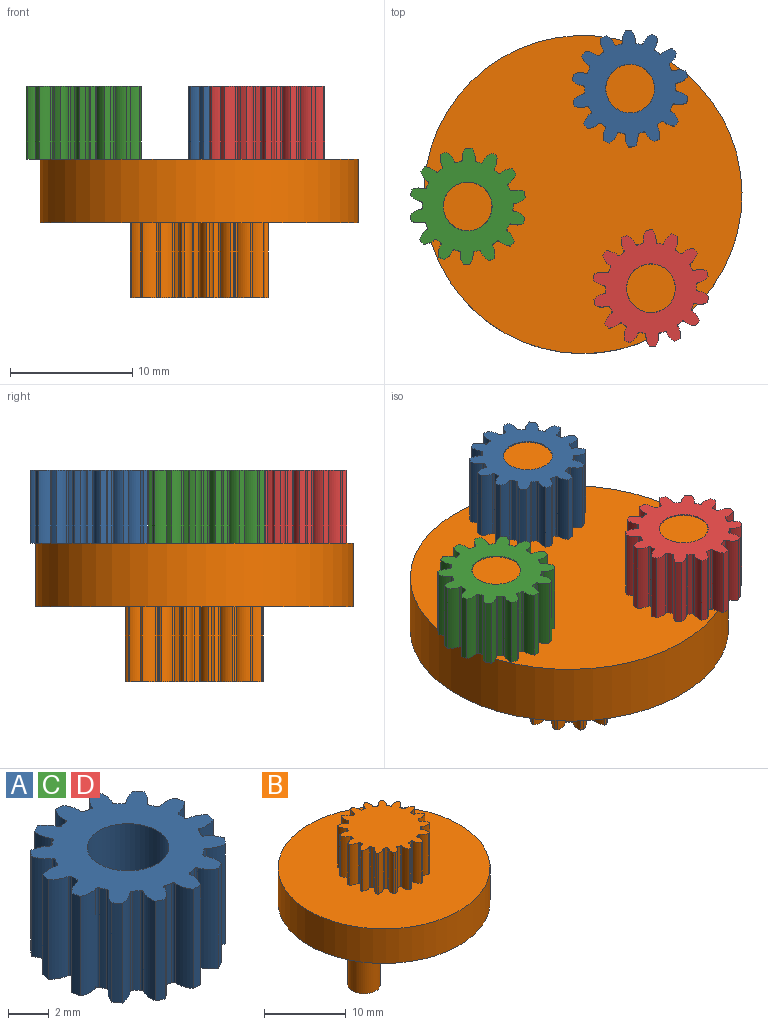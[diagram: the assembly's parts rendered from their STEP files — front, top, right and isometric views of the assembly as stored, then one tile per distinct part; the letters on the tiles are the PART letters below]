
ASSEMBLY  parts=4 mates=3
PART A: 87 faces, bbox 9.4x9.5x5.9 mm
  f0: cylinder r=0.13mm len=5.94mm, axis (0,0,-1), area 1.1mm2, adj f1,f84,f85,f86
  f1: cylinder r=3.71mm len=5.94mm, axis (0,0,-1), area 2.3mm2, adj f0,f2,f85,f86
  f2: cylinder r=0.13mm len=5.94mm, axis (0,0,-1), area 1.1mm2, adj f1,f3,f85,f86
  f3: cylinder r=1.52mm len=5.94mm, axis (0,0,-1), area 6.1mm2, adj f2,f4,f85,f86
  f4: cylinder r=4.76mm len=5.94mm, axis (0,0,-1), area 3mm2, adj f3,f5,f85,f86
  f5: cylinder r=1.52mm len=5.94mm, axis (0,0,-1), area 6.1mm2, adj f4,f6,f85,f86
  f6: cylinder r=0.13mm len=5.94mm, axis (0,0,-1), area 1.1mm2, adj f5,f7,f85,f86
  f7: cylinder r=3.71mm len=5.94mm, axis (0,0,-1), area 2.3mm2, adj f6,f8,f85,f86
  f8: cylinder r=0.13mm len=5.94mm, axis (0,0,-1), area 1.1mm2, adj f7,f9,f85,f86
  f9: cylinder r=1.52mm len=5.94mm, axis (0,0,-1), area 6.1mm2, adj f8,f10,f85,f86
  f10: cylinder r=4.76mm len=5.94mm, axis (0,0,-1), area 3mm2, adj f9,f11,f85,f86
  f11: cylinder r=1.52mm len=5.94mm, axis (0,0,-1), area 6.1mm2, adj f10,f12,f85,f86
  f12: cylinder r=0.13mm len=5.94mm, axis (0,0,-1), area 1.1mm2, adj f11,f13,f85,f86
  f13: cylinder r=3.71mm len=5.94mm, axis (0,0,-1), area 2.3mm2, adj f12,f14,f85,f86
  f14: cylinder r=0.13mm len=5.94mm, axis (0,0,-1), area 1.1mm2, adj f13,f15,f85,f86
  f15: cylinder r=1.52mm len=5.94mm, axis (0,0,-1), area 6.1mm2, adj f14,f16,f85,f86
  f16: cylinder r=4.76mm len=5.94mm, axis (0,0,-1), area 3mm2, adj f15,f17,f85,f86
  f17: cylinder r=1.52mm len=5.94mm, axis (0,0,-1), area 6.1mm2, adj f16,f18,f85,f86
  f18: cylinder r=0.13mm len=5.94mm, axis (0,0,-1), area 1.1mm2, adj f17,f19,f85,f86
  f19: cylinder r=3.71mm len=5.94mm, axis (0,0,-1), area 2.3mm2, adj f18,f20,f85,f86
  f20: cylinder r=0.13mm len=5.94mm, axis (0,0,-1), area 1.1mm2, adj f19,f21,f85,f86
  f21: cylinder r=1.52mm len=5.94mm, axis (0,0,-1), area 6.1mm2, adj f20,f22,f85,f86
  f22: cylinder r=4.76mm len=5.94mm, axis (0,0,-1), area 3mm2, adj f21,f23,f85,f86
  f23: cylinder r=1.52mm len=5.94mm, axis (0,0,-1), area 6.1mm2, adj f22,f24,f85,f86
  f24: cylinder r=0.13mm len=5.94mm, axis (0,0,-1), area 1.1mm2, adj f23,f25,f85,f86
  f25: cylinder r=3.71mm len=5.94mm, axis (0,0,-1), area 2.3mm2, adj f24,f26,f85,f86
  f26: cylinder r=0.13mm len=5.94mm, axis (0,0,-1), area 1.1mm2, adj f25,f27,f85,f86
  f27: cylinder r=1.52mm len=5.94mm, axis (0,0,-1), area 6.1mm2, adj f26,f28,f85,f86
  f28: cylinder r=4.76mm len=5.94mm, axis (0,0,-1), area 3mm2, adj f27,f29,f85,f86
  f29: cylinder r=1.52mm len=5.94mm, axis (0,0,-1), area 6.1mm2, adj f28,f30,f85,f86
  f30: cylinder r=0.13mm len=5.94mm, axis (0,0,-1), area 1.1mm2, adj f29,f31,f85,f86
  f31: cylinder r=3.71mm len=5.94mm, axis (0,0,-1), area 2.3mm2, adj f30,f32,f85,f86
  f32: cylinder r=0.13mm len=5.94mm, axis (0,0,-1), area 1.1mm2, adj f31,f33,f85,f86
  f33: cylinder r=1.52mm len=5.94mm, axis (0,0,-1), area 6.1mm2, adj f32,f34,f85,f86
  f34: cylinder r=4.76mm len=5.94mm, axis (0,0,-1), area 3mm2, adj f33,f35,f85,f86
  f35: cylinder r=1.52mm len=5.94mm, axis (0,0,-1), area 6.1mm2, adj f34,f36,f85,f86
  f36: cylinder r=0.13mm len=5.94mm, axis (0,0,-1), area 1.1mm2, adj f35,f37,f85,f86
  f37: cylinder r=3.71mm len=5.94mm, axis (0,0,-1), area 2.3mm2, adj f36,f38,f85,f86
  f38: cylinder r=0.13mm len=5.94mm, axis (0,0,-1), area 1.1mm2, adj f37,f39,f85,f86
  f39: cylinder r=1.52mm len=5.94mm, axis (0,0,-1), area 6.1mm2, adj f38,f40,f85,f86
  f40: cylinder r=4.76mm len=5.94mm, axis (0,0,-1), area 3mm2, adj f39,f41,f85,f86
  f41: cylinder r=1.52mm len=5.94mm, axis (0,0,-1), area 6.1mm2, adj f40,f42,f85,f86
  f42: cylinder r=0.13mm len=5.94mm, axis (0,0,-1), area 1.1mm2, adj f41,f43,f85,f86
  f43: cylinder r=3.71mm len=5.94mm, axis (0,0,-1), area 2.3mm2, adj f42,f44,f85,f86
  f44: cylinder r=0.13mm len=5.94mm, axis (0,0,-1), area 1.1mm2, adj f43,f45,f85,f86
  f45: cylinder r=1.52mm len=5.94mm, axis (0,0,-1), area 6.1mm2, adj f44,f46,f85,f86
  f46: cylinder r=4.76mm len=5.94mm, axis (0,0,-1), area 3mm2, adj f45,f47,f85,f86
  f47: cylinder r=1.52mm len=5.94mm, axis (0,0,-1), area 6.1mm2, adj f46,f48,f85,f86
  f48: cylinder r=0.13mm len=5.94mm, axis (0,0,-1), area 1.1mm2, adj f47,f49,f85,f86
  f49: cylinder r=3.71mm len=5.94mm, axis (0,0,-1), area 2.3mm2, adj f48,f50,f85,f86
  f50: cylinder r=0.13mm len=5.94mm, axis (0,0,-1), area 1.1mm2, adj f49,f51,f85,f86
  f51: cylinder r=1.52mm len=5.94mm, axis (0,0,-1), area 6.1mm2, adj f50,f52,f85,f86
  f52: cylinder r=4.76mm len=5.94mm, axis (0,0,-1), area 3mm2, adj f51,f53,f85,f86
  f53: cylinder r=1.52mm len=5.94mm, axis (0,0,-1), area 6.1mm2, adj f52,f54,f85,f86
  f54: cylinder r=0.13mm len=5.94mm, axis (0,0,-1), area 1.1mm2, adj f53,f55,f85,f86
  f55: cylinder r=3.71mm len=5.94mm, axis (0,0,-1), area 2.3mm2, adj f54,f56,f85,f86
  f56: cylinder r=0.13mm len=5.94mm, axis (0,0,-1), area 1.1mm2, adj f55,f57,f85,f86
  f57: cylinder r=1.52mm len=5.94mm, axis (0,0,-1), area 6.1mm2, adj f56,f58,f85,f86
  f58: cylinder r=4.76mm len=5.94mm, axis (0,0,-1), area 3mm2, adj f57,f59,f85,f86
  f59: cylinder r=1.52mm len=5.94mm, axis (0,0,-1), area 6.1mm2, adj f58,f60,f85,f86
  f60: cylinder r=0.13mm len=5.94mm, axis (0,0,-1), area 1.1mm2, adj f59,f61,f85,f86
  f61: cylinder r=3.71mm len=5.94mm, axis (0,0,-1), area 2.3mm2, adj f60,f62,f85,f86
  f62: cylinder r=0.13mm len=5.94mm, axis (0,0,-1), area 1.1mm2, adj f61,f63,f85,f86
  f63: cylinder r=1.52mm len=5.94mm, axis (0,0,-1), area 6.1mm2, adj f62,f64,f85,f86
  f64: cylinder r=4.76mm len=5.94mm, axis (0,0,-1), area 3mm2, adj f63,f65,f85,f86
  f65: cylinder r=1.52mm len=5.94mm, axis (0,0,-1), area 6.1mm2, adj f64,f66,f85,f86
  f66: cylinder r=0.13mm len=5.94mm, axis (0,0,-1), area 1.1mm2, adj f65,f67,f85,f86
  f67: cylinder r=3.71mm len=5.94mm, axis (0,0,-1), area 2.3mm2, adj f66,f68,f85,f86
  f68: cylinder r=0.13mm len=5.94mm, axis (0,0,-1), area 1.1mm2, adj f67,f69,f85,f86
  f69: cylinder r=1.52mm len=5.94mm, axis (0,0,-1), area 6.1mm2, adj f68,f70,f85,f86
  f70: cylinder r=4.76mm len=5.94mm, axis (0,0,-1), area 3mm2, adj f69,f71,f85,f86
  f71: cylinder r=1.52mm len=5.94mm, axis (0,0,-1), area 6.1mm2, adj f70,f72,f85,f86
  f72: cylinder r=0.13mm len=5.94mm, axis (0,0,-1), area 1.1mm2, adj f71,f73,f85,f86
  f73: cylinder r=3.71mm len=5.94mm, axis (0,0,-1), area 2.3mm2, adj f72,f74,f85,f86
  f74: cylinder r=0.13mm len=5.94mm, axis (0,0,-1), area 1.1mm2, adj f73,f75,f85,f86
  f75: cylinder r=1.52mm len=5.94mm, axis (0,0,-1), area 6.1mm2, adj f74,f76,f85,f86
  f76: cylinder r=4.76mm len=5.94mm, axis (0,0,-1), area 3mm2, adj f75,f77,f85,f86
  f77: cylinder r=1.52mm len=5.94mm, axis (0,0,-1), area 6.1mm2, adj f76,f78,f85,f86
  f78: cylinder r=0.13mm len=5.94mm, axis (0,0,-1), area 1.1mm2, adj f77,f79,f85,f86
  f79: cylinder r=3.71mm len=5.94mm, axis (0,0,-1), area 2.3mm2, adj f78,f80,f85,f86
  f80: cylinder r=0.13mm len=5.94mm, axis (0,0,-1), area 1.1mm2, adj f79,f81,f85,f86
  f81: cylinder r=1.52mm len=5.94mm, axis (0,0,-1), area 6.1mm2, adj f80,f82,f85,f86
  f82: cylinder r=4.76mm len=5.94mm, axis (0,0,-1), area 3mm2, adj f81,f84,f85,f86
  f83: cylinder r=1.99mm len=5.94mm, axis (0,0,-1), area 74.5mm2, adj f85,f86
  f84: cylinder r=1.52mm len=5.94mm, axis (0,0,-1), area 6.1mm2, adj f0,f82,f85,f86
  f85: plane 9.53x9.39mm, normal (0,0,1), area 44.4mm2, adj f0,f1,f2,f3,f4,f5,f6,f7
  f86: plane 9.53x9.39mm, normal (0,0,-1), area 44.4mm2, adj f0,f1,f2,f3,f4,f5,f6,f7
PART B: 112 faces, bbox 26x26x17.2 mm
  f0: plane 25.98x25.98mm, normal (0,0,1), area 450.4mm2, adj f1,f9,f10,f11,f12,f13,f14,f15
  f1: cylinder r=12.99mm len=25.98mm, axis (0,0,-1), area 423mm2, adj f0,f2
  f2: plane 25.98x25.98mm, normal (0,0,-1), area 493.3mm2, adj f1,f3,f5,f7
  f3: cylinder r=1.98mm len=5.87mm, axis (0,0,1), area 73mm2, adj f2,f4
  f4: plane 3.96x3.96mm, normal (0,0,-1), area 12.3mm2, adj f3
  f5: cylinder r=1.98mm len=5.87mm, axis (0,0,1), area 73mm2, adj f2,f6
  f6: plane 3.96x3.96mm, normal (0,0,-1), area 12.3mm2, adj f5
  f7: cylinder r=1.98mm len=5.87mm, axis (0,0,1), area 73mm2, adj f2,f8
  f8: plane 3.96x3.96mm, normal (0,0,-1), area 12.3mm2, adj f7
  f9: cylinder r=0.13mm len=6.12mm, axis (0,0,-1), area 1.1mm2, adj f0,f10,f110,f111
  f10: cylinder r=4.48mm len=6.12mm, axis (0,0,-1), area 2.3mm2, adj f0,f9,f11,f111
  f11: cylinder r=0.13mm len=6.12mm, axis (0,0,-1), area 1.1mm2, adj f0,f10,f12,f111
  f12: cylinder r=1.52mm len=6.12mm, axis (0,0,-1), area 7.2mm2, adj f0,f11,f13,f111
  f13: cylinder r=5.65mm len=6.12mm, axis (0,0,-1), area 1.6mm2, adj f0,f12,f14,f111
  f14: cylinder r=1.52mm len=6.12mm, axis (0,0,-1), area 7.2mm2, adj f0,f13,f15,f111
  f15: cylinder r=0.13mm len=6.12mm, axis (0,0,-1), area 1.1mm2, adj f0,f14,f16,f111
  f16: cylinder r=4.48mm len=6.12mm, axis (0,0,-1), area 2.3mm2, adj f0,f15,f17,f111
  f17: cylinder r=0.13mm len=6.12mm, axis (0,0,-1), area 1.1mm2, adj f0,f16,f18,f111
  f18: cylinder r=1.52mm len=6.12mm, axis (0,0,-1), area 7.2mm2, adj f0,f17,f19,f111
  f19: cylinder r=5.65mm len=6.12mm, axis (0,0,-1), area 1.6mm2, adj f0,f18,f20,f111
  f20: cylinder r=1.52mm len=6.12mm, axis (0,0,-1), area 7.2mm2, adj f0,f19,f21,f111
  f21: cylinder r=0.13mm len=6.12mm, axis (0,0,-1), area 1.1mm2, adj f0,f20,f22,f111
  f22: cylinder r=4.48mm len=6.12mm, axis (0,0,-1), area 2.3mm2, adj f0,f21,f23,f111
  f23: cylinder r=0.13mm len=6.12mm, axis (0,0,-1), area 1.1mm2, adj f0,f22,f24,f111
  f24: cylinder r=1.52mm len=6.12mm, axis (0,0,-1), area 7.2mm2, adj f0,f23,f25,f111
  f25: cylinder r=5.65mm len=6.12mm, axis (0,0,-1), area 1.6mm2, adj f0,f24,f26,f111
  f26: cylinder r=1.52mm len=6.12mm, axis (0,0,-1), area 7.2mm2, adj f0,f25,f27,f111
  f27: cylinder r=0.13mm len=6.12mm, axis (0,0,-1), area 1.1mm2, adj f0,f26,f28,f111
  f28: cylinder r=4.48mm len=6.12mm, axis (0,0,-1), area 2.3mm2, adj f0,f27,f29,f111
  f29: cylinder r=0.13mm len=6.12mm, axis (0,0,-1), area 1.1mm2, adj f0,f28,f30,f111
  f30: cylinder r=1.52mm len=6.12mm, axis (0,0,-1), area 7.2mm2, adj f0,f29,f31,f111
  f31: cylinder r=5.65mm len=6.12mm, axis (0,0,-1), area 1.6mm2, adj f0,f30,f32,f111
  f32: cylinder r=1.52mm len=6.12mm, axis (0,0,-1), area 7.2mm2, adj f0,f31,f33,f111
  f33: cylinder r=0.13mm len=6.12mm, axis (0,0,-1), area 1.1mm2, adj f0,f32,f34,f111
  f34: cylinder r=4.48mm len=6.12mm, axis (0,0,-1), area 2.3mm2, adj f0,f33,f35,f111
  f35: cylinder r=0.13mm len=6.12mm, axis (0,0,-1), area 1.1mm2, adj f0,f34,f36,f111
  f36: cylinder r=1.52mm len=6.12mm, axis (0,0,-1), area 7.2mm2, adj f0,f35,f37,f111
  f37: cylinder r=5.65mm len=6.12mm, axis (0,0,-1), area 1.6mm2, adj f0,f36,f38,f111
  f38: cylinder r=1.52mm len=6.12mm, axis (0,0,-1), area 7.2mm2, adj f0,f37,f39,f111
  f39: cylinder r=0.13mm len=6.12mm, axis (0,0,-1), area 1.1mm2, adj f0,f38,f40,f111
  f40: cylinder r=4.48mm len=6.12mm, axis (0,0,-1), area 2.3mm2, adj f0,f39,f41,f111
  f41: cylinder r=0.13mm len=6.12mm, axis (0,0,-1), area 1.1mm2, adj f0,f40,f42,f111
  f42: cylinder r=1.52mm len=6.12mm, axis (0,0,-1), area 7.2mm2, adj f0,f41,f43,f111
  f43: cylinder r=5.65mm len=6.12mm, axis (0,0,-1), area 1.6mm2, adj f0,f42,f44,f111
  f44: cylinder r=1.52mm len=6.12mm, axis (0,0,-1), area 7.2mm2, adj f0,f43,f45,f111
  f45: cylinder r=0.13mm len=6.12mm, axis (0,0,-1), area 1.1mm2, adj f0,f44,f46,f111
  f46: cylinder r=4.48mm len=6.12mm, axis (0,0,-1), area 2.3mm2, adj f0,f45,f47,f111
  f47: cylinder r=0.13mm len=6.12mm, axis (0,0,-1), area 1.1mm2, adj f0,f46,f48,f111
  f48: cylinder r=1.52mm len=6.12mm, axis (0,0,-1), area 7.2mm2, adj f0,f47,f49,f111
  f49: cylinder r=5.65mm len=6.12mm, axis (0,0,-1), area 1.6mm2, adj f0,f48,f50,f111
  f50: cylinder r=1.52mm len=6.12mm, axis (0,0,-1), area 7.2mm2, adj f0,f49,f51,f111
  f51: cylinder r=0.13mm len=6.12mm, axis (0,0,-1), area 1.1mm2, adj f0,f50,f52,f111
  f52: cylinder r=4.48mm len=6.12mm, axis (0,0,-1), area 2.3mm2, adj f0,f51,f53,f111
  f53: cylinder r=0.13mm len=6.12mm, axis (0,0,-1), area 1.1mm2, adj f0,f52,f54,f111
  f54: cylinder r=1.52mm len=6.12mm, axis (0,0,-1), area 7.2mm2, adj f0,f53,f55,f111
  f55: cylinder r=5.65mm len=6.12mm, axis (0,0,-1), area 1.6mm2, adj f0,f54,f56,f111
  f56: cylinder r=1.52mm len=6.12mm, axis (0,0,-1), area 7.2mm2, adj f0,f55,f57,f111
  f57: cylinder r=0.13mm len=6.12mm, axis (0,0,-1), area 1.1mm2, adj f0,f56,f58,f111
  f58: cylinder r=4.48mm len=6.12mm, axis (0,0,-1), area 2.3mm2, adj f0,f57,f59,f111
  f59: cylinder r=0.13mm len=6.12mm, axis (0,0,-1), area 1.1mm2, adj f0,f58,f60,f111
  f60: cylinder r=1.52mm len=6.12mm, axis (0,0,-1), area 7.2mm2, adj f0,f59,f61,f111
  f61: cylinder r=5.65mm len=6.12mm, axis (0,0,-1), area 1.6mm2, adj f0,f60,f62,f111
  f62: cylinder r=1.52mm len=6.12mm, axis (0,0,-1), area 7.2mm2, adj f0,f61,f63,f111
  f63: cylinder r=0.13mm len=6.12mm, axis (0,0,-1), area 1.1mm2, adj f0,f62,f64,f111
  f64: cylinder r=4.48mm len=6.12mm, axis (0,0,-1), area 2.3mm2, adj f0,f63,f65,f111
  f65: cylinder r=0.13mm len=6.12mm, axis (0,0,-1), area 1.1mm2, adj f0,f64,f66,f111
  f66: cylinder r=1.52mm len=6.12mm, axis (0,0,-1), area 7.2mm2, adj f0,f65,f67,f111
  f67: cylinder r=5.65mm len=6.12mm, axis (0,0,-1), area 1.6mm2, adj f0,f66,f68,f111
  f68: cylinder r=1.52mm len=6.12mm, axis (0,0,-1), area 7.2mm2, adj f0,f67,f69,f111
  f69: cylinder r=0.13mm len=6.12mm, axis (0,0,-1), area 1.1mm2, adj f0,f68,f70,f111
  f70: cylinder r=4.48mm len=6.12mm, axis (0,0,-1), area 2.3mm2, adj f0,f69,f71,f111
  f71: cylinder r=0.13mm len=6.12mm, axis (0,0,-1), area 1.1mm2, adj f0,f70,f72,f111
  f72: cylinder r=1.52mm len=6.12mm, axis (0,0,-1), area 7.2mm2, adj f0,f71,f73,f111
  f73: cylinder r=5.65mm len=6.12mm, axis (0,0,-1), area 1.6mm2, adj f0,f72,f74,f111
  f74: cylinder r=1.52mm len=6.12mm, axis (0,0,-1), area 7.2mm2, adj f0,f73,f75,f111
  f75: cylinder r=0.13mm len=6.12mm, axis (0,0,-1), area 1.1mm2, adj f0,f74,f76,f111
  f76: cylinder r=4.48mm len=6.12mm, axis (0,0,-1), area 2.3mm2, adj f0,f75,f77,f111
  f77: cylinder r=0.13mm len=6.12mm, axis (0,0,-1), area 1.1mm2, adj f0,f76,f78,f111
  f78: cylinder r=1.52mm len=6.12mm, axis (0,0,-1), area 7.2mm2, adj f0,f77,f79,f111
  f79: cylinder r=5.65mm len=6.12mm, axis (0,0,-1), area 1.6mm2, adj f0,f78,f80,f111
  f80: cylinder r=1.52mm len=6.12mm, axis (0,0,-1), area 7.2mm2, adj f0,f79,f81,f111
  f81: cylinder r=0.13mm len=6.12mm, axis (0,0,-1), area 1.1mm2, adj f0,f80,f82,f111
  f82: cylinder r=4.48mm len=6.12mm, axis (0,0,-1), area 2.3mm2, adj f0,f81,f83,f111
  f83: cylinder r=0.13mm len=6.12mm, axis (0,0,-1), area 1.1mm2, adj f0,f82,f84,f111
  f84: cylinder r=1.52mm len=6.12mm, axis (0,0,-1), area 7.2mm2, adj f0,f83,f85,f111
  f85: cylinder r=5.65mm len=6.12mm, axis (0,0,-1), area 1.6mm2, adj f0,f84,f86,f111
  f86: cylinder r=1.52mm len=6.12mm, axis (0,0,-1), area 7.2mm2, adj f0,f85,f87,f111
  f87: cylinder r=0.13mm len=6.12mm, axis (0,0,-1), area 1.1mm2, adj f0,f86,f88,f111
  f88: cylinder r=4.48mm len=6.12mm, axis (0,0,-1), area 2.3mm2, adj f0,f87,f89,f111
  f89: cylinder r=0.13mm len=6.12mm, axis (0,0,-1), area 1.1mm2, adj f0,f88,f90,f111
  f90: cylinder r=1.52mm len=6.12mm, axis (0,0,-1), area 7.2mm2, adj f0,f89,f91,f111
  f91: cylinder r=5.65mm len=6.12mm, axis (0,0,-1), area 1.6mm2, adj f0,f90,f92,f111
  f92: cylinder r=1.52mm len=6.12mm, axis (0,0,-1), area 7.2mm2, adj f0,f91,f93,f111
  f93: cylinder r=0.13mm len=6.12mm, axis (0,0,-1), area 1.1mm2, adj f0,f92,f94,f111
  f94: cylinder r=4.48mm len=6.12mm, axis (0,0,-1), area 2.3mm2, adj f0,f93,f95,f111
  f95: cylinder r=0.13mm len=6.12mm, axis (0,0,-1), area 1.1mm2, adj f0,f94,f96,f111
  f96: cylinder r=1.52mm len=6.12mm, axis (0,0,-1), area 7.2mm2, adj f0,f95,f97,f111
  f97: cylinder r=5.65mm len=6.12mm, axis (0,0,-1), area 1.6mm2, adj f0,f96,f98,f111
  f98: cylinder r=1.52mm len=6.12mm, axis (0,0,-1), area 7.2mm2, adj f0,f97,f99,f111
  f99: cylinder r=0.13mm len=6.12mm, axis (0,0,-1), area 1.1mm2, adj f0,f98,f100,f111
  f100: cylinder r=4.48mm len=6.12mm, axis (0,0,-1), area 2.3mm2, adj f0,f99,f101,f111
  f101: cylinder r=0.13mm len=6.12mm, axis (0,0,-1), area 1.1mm2, adj f0,f100,f102,f111
  f102: cylinder r=1.52mm len=6.12mm, axis (0,0,-1), area 7.2mm2, adj f0,f101,f103,f111
  f103: cylinder r=5.65mm len=6.12mm, axis (0,0,-1), area 1.6mm2, adj f0,f102,f104,f111
  f104: cylinder r=1.52mm len=6.12mm, axis (0,0,-1), area 7.2mm2, adj f0,f103,f105,f111
  f105: cylinder r=0.13mm len=6.12mm, axis (0,0,-1), area 1.1mm2, adj f0,f104,f106,f111
  f106: cylinder r=4.48mm len=6.12mm, axis (0,0,-1), area 2.3mm2, adj f0,f105,f107,f111
  f107: cylinder r=0.13mm len=6.12mm, axis (0,0,-1), area 1.1mm2, adj f0,f106,f108,f111
  f108: cylinder r=1.52mm len=6.12mm, axis (0,0,-1), area 7.2mm2, adj f0,f107,f109,f111
  f109: cylinder r=5.65mm len=6.12mm, axis (0,0,-1), area 1.6mm2, adj f0,f108,f110,f111
  f110: cylinder r=1.52mm len=6.12mm, axis (0,0,-1), area 7.2mm2, adj f0,f9,f109,f111
  f111: plane 11.28x11.23mm, normal (0,0,1), area 79.9mm2, adj f9,f10,f11,f12,f13,f14,f15,f16
PART C: same geometry as A
PART D: same geometry as A
PLACE A rot(axis=(0.98,-0.21,0),180deg) t=(-10.63,37.55,8.72)mm
PLACE B rot(axis=(-0.21,-0.98,0),180deg) t=(-14.49,28.9,2.78)mm
PLACE C rot(axis=(-0.23,-0.97,0),180deg) t=(-23.9,27.92,8.72)mm
PLACE D rot(axis=(0,0,1),155.9deg) t=(-8.93,21.24,2.78)mm
MATE revolute B.f5 <-> D.f1  axis (0,0,1) through (-8.93,21.24,2.78)mm
MATE revolute A.f1 <-> B.f3  axis (0,0,-1) through (-10.63,37.55,2.78)mm
MATE revolute C.f1 <-> B.f7  axis (0,0,-1) through (-23.9,27.92,2.78)mm
